# Revit family: Table-Teknion-ATMJ_Circular_Square_Meeting_Table-R2022
name_source: partatom
category: Furniture
units: mm (PartAtom-declared; Revit-internal decimal feet)

## family parameters
Always vertical = Yes
Cut with Voids When Loaded = No
Enable Cutting in Views = No
OmniClass Number = 23.40.20.00
OmniClass Title = General Furniture and Specialties
Render Appearance Source = Family Geometry
Room Calculation Point = No
Shared = Yes
Work Plane-Based = No

## types (4) — shared parameters
Assembly Code = E2020200
Manufacturer = Teknion
Manufacturer Fax = 416.661.4586
Part Number = ATMJ
Product Documentation Link = http://www.teknion.com
Product Line = Meeting Tables
Product Page URL = https://www.teknion.com
Series = Audience Boardroom & Meeting Tables
Sustainability Data = https://www.teknion.com
URL = www.teknion.com
Unit Weight URL = http://www.teknion.com
Warranty = http://www.teknion.com
zero-valued in all types: Default Elevation

## per-type parameters (varying)
| type | 2D - P & M | 2D - S & C | C - Stretch Leg With Caster | Description | M - Fixed Post Leg With Caster | Model | P - Fixed Post Leg | S - Stretch Leg |
| Fixed Post Leg Base | Yes | No | No | Circular Meeting Table, Fixed Post Leg Base | No | ATMJP__ | Yes | No |
| Stretch Leg Base | No | Yes | No | Circular Meeting Table, Stretch Leg Base | No | ATMJS__ | No | Yes |
| Fixed Post Leg With Caster Base | Yes | No | No | Circular Meeting Table, Fixed Post Leg With Caster Base | Yes | ATMJM__ | No | No |
| Stretch Leg With Caster Base | No | Yes | Yes | Circular Meeting Table, Stretch Leg With Caster Base | No | ATMJC__ | No | No |

## geometry (parser evidence)
native form markers: Sweep x14
no freeform markers — native parametric forms only
